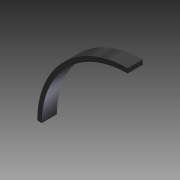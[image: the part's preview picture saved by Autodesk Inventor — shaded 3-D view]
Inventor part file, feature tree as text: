
AUTODESK INVENTOR PART (.ipt)
format: ipt  version: 2014 SP1 (Build 180222100, 222)  size: 74,752 bytes
history: native  units: in
note: dims shown in document units (in); Inventor stores cm internally (conversion verified against a paired STEP export)
features: extrude x1, sketch x1
ambient origin geometry x8: Origin, YZ Plane, XZ Plane, XY Plane, X Axis, Y Axis, Z Axis, Center Point
bodies: Solid1 (feature_tree)
feature tree (2):
  extrude  "Extrusion1"  Depth=2.5in
  sketch  "Sketch1"  dims[d0=30.0in d1=0.75in d2=2.5in d3=0.0in]
